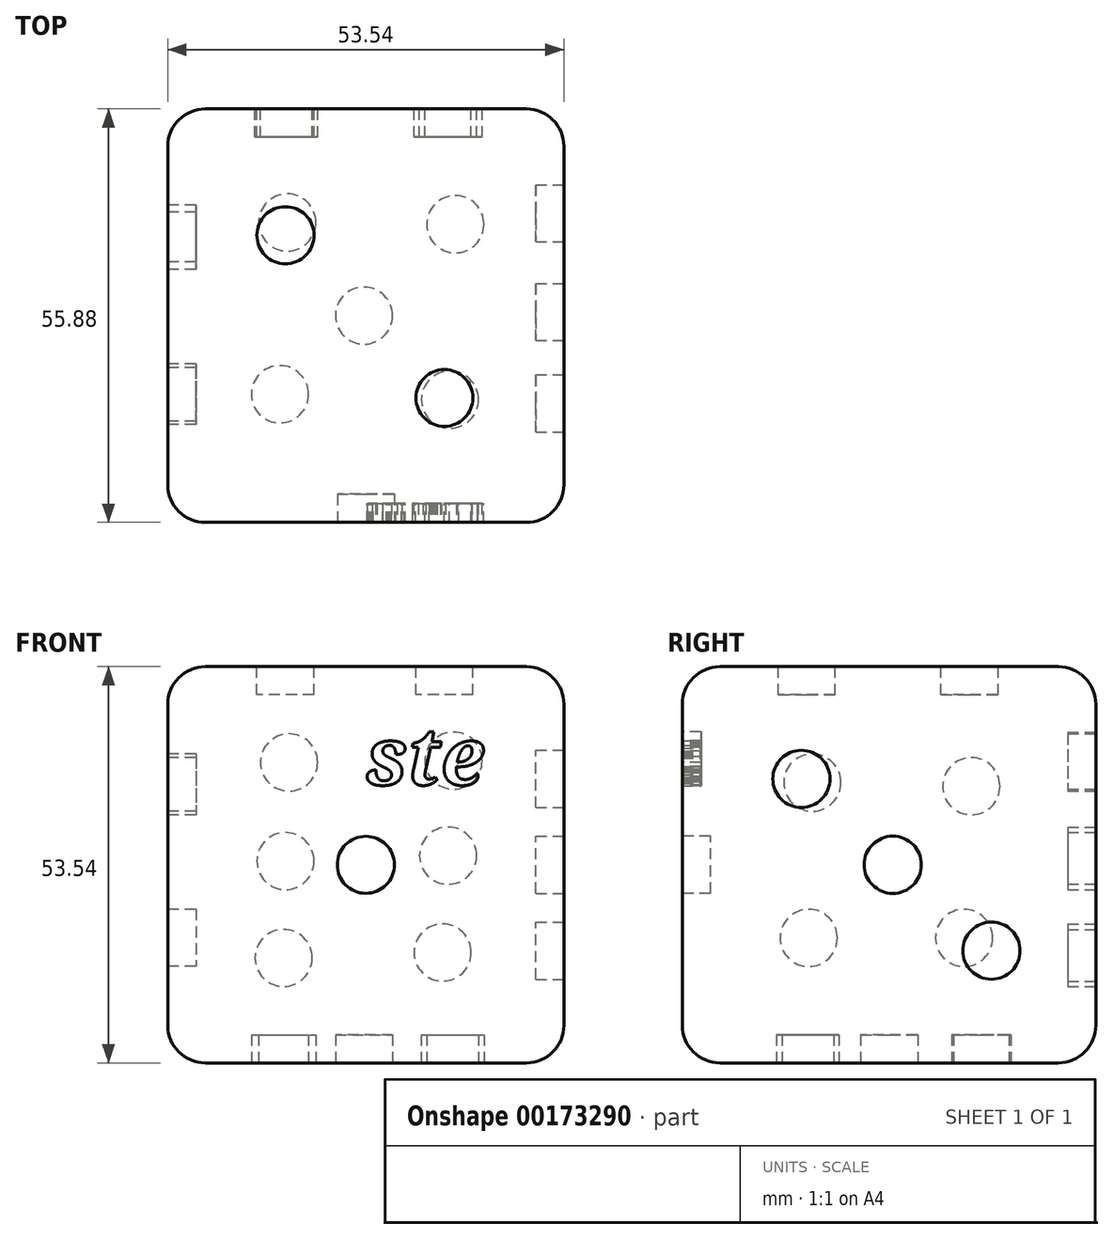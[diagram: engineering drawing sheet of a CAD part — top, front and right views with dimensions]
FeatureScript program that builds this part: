
annotation { "Feature Type Name" : "Feature", "Feature Type Description" : "" }
export const myFeature = defineFeature(function(context is Context, id is Id, definition is map)
    precondition{}
    {
        {
            var Q0;
            Q0=qCreatedBy(makeId("Front.planeOp"),FACE);
            var sketch = newSketch(context, id + "F0", { "sketchPlane" : qUnion([Q0])});
            skCircle(sketch, "E0.cCircle", {"center": v(0, 0) * mm, "radius": 26.77 * mm, "construction": true});
            skLineSegment(sketch, "E0.0", {"start": v(26.77, 26.77) * mm, "end": v(26.77, -26.77) * mm});
            skLineSegment(sketch, "E0.1", {"start": v(26.77, -26.77) * mm, "end": v(-26.77, -26.77) * mm});
            skLineSegment(sketch, "E0.2", {"start": v(-26.77, -26.77) * mm, "end": v(-26.77, 26.77) * mm});
            skLineSegment(sketch, "E0.3", {"start": v(-26.77, 26.77) * mm, "end": v(26.77, 26.77) * mm});
            skPoint(sketch, "E0.0.midPoint", {"position": v(26.77, 0) * mm});
            skSolve(sketch);
        }
        {
            var Q0;
            Q0 = qSketchRegion(id + "F0", true);
            extrude(context, id + "F1", {"entities" : qUnion([Q0]), "endBound" : BoundingType.SYMMETRIC, "depth" : 55.88 * mm});
        }
        {
            var Q0;
            Q0=makeQuery(id+"F1.opExtrude","SWEPT_FACE",FACE,{"disambiguationData":[OSD([sQuery(id+"F0.wireOp",EDGE,"E0.2")])]});
            var Q1;
            Q1=makeQuery(id+"F1.opExtrude","SWEPT_FACE",FACE,{"disambiguationData":[OSD([sQuery(id+"F0.wireOp",EDGE,"E0.1")])]});
            var Q2;
            Q2=makeQuery(id+"F1.opExtrude","CAP_FACE",FACE,{"disambiguationData":[OSD([sQuery(id+"F0.wireOp",EDGE,"E0.0"),sQuery(id+"F0.wireOp",EDGE,"E0.1"),sQuery(id+"F0.wireOp",EDGE,"E0.2"),sQuery(id+"F0.wireOp",EDGE,"E0.3")])],"isStart":false});
            var Q3;
            Q3=makeQuery(id+"F1.opExtrude","SWEPT_FACE",FACE,{"disambiguationData":[OSD([sQuery(id+"F0.wireOp",EDGE,"E0.3")])]});
            var Q4;
            Q4=makeQuery(id+"F1.opExtrude","CAP_FACE",FACE,{"disambiguationData":[OSD([sQuery(id+"F0.wireOp",EDGE,"E0.0"),sQuery(id+"F0.wireOp",EDGE,"E0.1"),sQuery(id+"F0.wireOp",EDGE,"E0.2"),sQuery(id+"F0.wireOp",EDGE,"E0.3")])],"isStart":true});
            fillet(context, id + "F2", {"entities" : qUnion([Q0, Q1, Q2, Q3, Q4]), "radius" : 5.08 * mm, "tangentPropagation" : true, "allowEdgeOverflow" : false});
        }
        {
            var Q0;
            Q0=makeQuery(id+"F1.opExtrude","CAP_FACE",FACE,{"disambiguationData":[OSD([sQuery(id+"F0.wireOp",EDGE,"E0.0"),sQuery(id+"F0.wireOp",EDGE,"E0.1"),sQuery(id+"F0.wireOp",EDGE,"E0.2"),sQuery(id+"F0.wireOp",EDGE,"E0.3")])],"isStart":false});
            var sketch = newSketch(context, id + "F3", { "sketchPlane" : qUnion([Q0])});
            skCircle(sketch, "E1", {"center": v(0, 0) * mm, "radius": 3.86 * mm});
            skSolve(sketch);
        }
        {
            var Q0;
            Q0 = qSketchRegion(id + "F3", true);
            extrude(context, id + "F4", {"entities" : qUnion([Q0]), "operationType" : NewBodyOperationType.REMOVE, "oppositeDirection" : true, "depth" : 3.8 * mm});
        }
        {
            var Q0;
            Q0=makeQuery(id+"F1.opExtrude","SWEPT_FACE",FACE,{"disambiguationData":[OSD([sQuery(id+"F0.wireOp",EDGE,"E0.3")])]});
            var sketch = newSketch(context, id + "F5", { "sketchPlane" : qUnion([Q0])});
            skCircle(sketch, "E2", {"center": v(-10.87, 10.87) * mm, "radius": 3.86 * mm});
            skCircle(sketch, "E3", {"center": v(10.62, -11.11) * mm, "radius": 3.84 * mm});
            skSolve(sketch);
        }
        {
            var Q0;
            Q0 = qSketchRegion(id + "F5", true);
            extrude(context, id + "F6", {"entities" : qUnion([Q0]), "operationType" : NewBodyOperationType.REMOVE, "oppositeDirection" : true, "depth" : 3.8 * mm});
        }
        {
            var Q0;
            Q0=makeQuery(id+"F1.opExtrude","SWEPT_FACE",FACE,{"disambiguationData":[OSD([sQuery(id+"F0.wireOp",EDGE,"E0.0")])]});
            var sketch = newSketch(context, id + "F7", { "sketchPlane" : qUnion([Q0])});
            skCircle(sketch, "E4", {"center": v(-11.85, 11.6) * mm, "radius": 3.87 * mm});
            skCircle(sketch, "E5", {"center": v(0.5, 0) * mm, "radius": 3.87 * mm});
            skCircle(sketch, "E6", {"center": v(13.83, -11.6) * mm, "radius": 3.87 * mm});
            skSolve(sketch);
        }
        {
            var Q0;
            Q0=makeQuery(id+"F7.imprint","IMPRINT",FACE,{"disambiguationData":[TD([[makeQuery(id+"F7.imprint","IMPRINT",EDGE,{"derivedFrom":sQuery(id+"F7.wireOp",EDGE,"E4")}),1.0]])]});
            var Q1;
            Q1=makeQuery(id+"F7.imprint","IMPRINT",FACE,{"disambiguationData":[TD([[makeQuery(id+"F7.imprint","IMPRINT",EDGE,{"derivedFrom":sQuery(id+"F7.wireOp",EDGE,"E5")}),1.0]])]});
            var Q2;
            Q2=makeQuery(id+"F7.imprint","IMPRINT",FACE,{"disambiguationData":[TD([[makeQuery(id+"F7.imprint","IMPRINT",EDGE,{"derivedFrom":sQuery(id+"F7.wireOp",EDGE,"E6")}),1.0]])]});
            var Q3;
            Q3=sQuery(id+"F7.wireOp",EDGE,"E6");
            var Q4;
            Q4=sQuery(id+"F7.wireOp",EDGE,"E4");
            var Q5;
            Q5=sQuery(id+"F7.wireOp",EDGE,"E5");
            extrude(context, id + "F8", {"entities" : qUnion([Q0, Q1, Q2]), "operationType" : NewBodyOperationType.REMOVE, "surfaceEntities" : qUnion([Q3, Q4, Q5]), "oppositeDirection" : true, "depth" : 3.8 * mm});
        }
        {
            var Q0;
            Q0=makeQuery(id+"F1.opExtrude","SWEPT_FACE",FACE,{"disambiguationData":[OSD([sQuery(id+"F0.wireOp",EDGE,"E0.2")])]});
            var sketch = newSketch(context, id + "F9", { "sketchPlane" : qUnion([Q0])});
            skCircle(sketch, "E7", {"center": v(-11.11, 10.62) * mm, "radius": 3.87 * mm});
            skCircle(sketch, "E8", {"center": v(10.37, 11.11) * mm, "radius": 3.87 * mm});
            skCircle(sketch, "E9", {"center": v(-10.12, -9.88) * mm, "radius": 3.87 * mm});
            skCircle(sketch, "E10", {"center": v(10.87, -9.88) * mm, "radius": 3.87 * mm});
            skSolve(sketch);
        }
        {
            var Q0;
            Q0=makeQuery(id+"F9.imprint","IMPRINT",FACE,{"disambiguationData":[TD([[makeQuery(id+"F9.imprint","IMPRINT",EDGE,{"derivedFrom":sQuery(id+"F9.wireOp",EDGE,"E7")}),1.0]])]});
            var Q1;
            Q1=makeQuery(id+"F9.imprint","IMPRINT",FACE,{"disambiguationData":[TD([[makeQuery(id+"F9.imprint","IMPRINT",EDGE,{"derivedFrom":sQuery(id+"F9.wireOp",EDGE,"E8")}),1.0]])]});
            var Q2;
            Q2=makeQuery(id+"F9.imprint","IMPRINT",FACE,{"disambiguationData":[TD([[makeQuery(id+"F9.imprint","IMPRINT",EDGE,{"derivedFrom":sQuery(id+"F9.wireOp",EDGE,"E9")}),1.0]])]});
            var Q3;
            Q3=makeQuery(id+"F9.imprint","IMPRINT",FACE,{"disambiguationData":[TD([[makeQuery(id+"F9.imprint","IMPRINT",EDGE,{"derivedFrom":sQuery(id+"F9.wireOp",EDGE,"E10")}),1.0]])]});
            var Q4;
            Q4=sQuery(id+"F9.wireOp",EDGE,"E10");
            var Q5;
            Q5=sQuery(id+"F9.wireOp",EDGE,"E8");
            extrude(context, id + "F10", {"entities" : qUnion([Q0, Q1, Q2, Q3]), "operationType" : NewBodyOperationType.REMOVE, "surfaceEntities" : qUnion([Q4, Q5]), "oppositeDirection" : true, "depth" : 3.8 * mm});
        }
        {
            var Q0;
            Q0=makeQuery(id+"F1.opExtrude","SWEPT_FACE",FACE,{"disambiguationData":[OSD([sQuery(id+"F0.wireOp",EDGE,"E0.1")])]});
            var sketch = newSketch(context, id + "F11", { "sketchPlane" : qUnion([Q0])});
            skCircle(sketch, "E11", {"center": v(-11.6, 10.62) * mm, "radius": 3.87 * mm});
            skCircle(sketch, "E12", {"center": v(11.36, 11.36) * mm, "radius": 3.87 * mm});
            skCircle(sketch, "E13", {"center": v(-10.62, -12.6) * mm, "radius": 3.87 * mm});
            skCircle(sketch, "E14", {"center": v(-0.25, 0) * mm, "radius": 3.87 * mm});
            skCircle(sketch, "E15", {"center": v(12.1, -12.35) * mm, "radius": 3.87 * mm});
            skSolve(sketch);
        }
        {
            var Q0;
            Q0=makeQuery(id+"F11.imprint","IMPRINT",FACE,{"disambiguationData":[TD([[makeQuery(id+"F11.imprint","IMPRINT",EDGE,{"derivedFrom":sQuery(id+"F11.wireOp",EDGE,"E11")}),1.0]])]});
            var Q1;
            Q1=makeQuery(id+"F11.imprint","IMPRINT",FACE,{"disambiguationData":[TD([[makeQuery(id+"F11.imprint","IMPRINT",EDGE,{"derivedFrom":sQuery(id+"F11.wireOp",EDGE,"E12")}),1.0]])]});
            var Q2;
            Q2=makeQuery(id+"F11.imprint","IMPRINT",FACE,{"disambiguationData":[TD([[makeQuery(id+"F11.imprint","IMPRINT",EDGE,{"derivedFrom":sQuery(id+"F11.wireOp",EDGE,"E14")}),1.0]])]});
            var Q3;
            Q3=makeQuery(id+"F11.imprint","IMPRINT",FACE,{"disambiguationData":[TD([[makeQuery(id+"F11.imprint","IMPRINT",EDGE,{"derivedFrom":sQuery(id+"F11.wireOp",EDGE,"E13")}),1.0]])]});
            var Q4;
            Q4=makeQuery(id+"F11.imprint","IMPRINT",FACE,{"disambiguationData":[TD([[makeQuery(id+"F11.imprint","IMPRINT",EDGE,{"derivedFrom":sQuery(id+"F11.wireOp",EDGE,"E15")}),1.0]])]});
            var Q5;
            Q5=sQuery(id+"F11.wireOp",EDGE,"E15");
            var Q6;
            Q6=sQuery(id+"F11.wireOp",EDGE,"E11");
            var Q7;
            Q7=sQuery(id+"F11.wireOp",EDGE,"E12");
            var Q8;
            Q8=sQuery(id+"F11.wireOp",EDGE,"E14");
            var Q9;
            Q9=sQuery(id+"F11.wireOp",EDGE,"E13");
            extrude(context, id + "F12", {"entities" : qUnion([Q0, Q1, Q2, Q3, Q4]), "operationType" : NewBodyOperationType.REMOVE, "surfaceEntities" : qUnion([Q5, Q6, Q7, Q8, Q9]), "oppositeDirection" : true, "depth" : 3.8 * mm});
        }
        {
            var Q0;
            Q0=makeQuery(id+"F1.opExtrude","CAP_FACE",FACE,{"disambiguationData":[OSD([sQuery(id+"F0.wireOp",EDGE,"E0.0"),sQuery(id+"F0.wireOp",EDGE,"E0.1"),sQuery(id+"F0.wireOp",EDGE,"E0.2"),sQuery(id+"F0.wireOp",EDGE,"E0.3")])],"isStart":true});
            var sketch = newSketch(context, id + "F13", { "sketchPlane" : qUnion([Q0])});
            skCircle(sketch, "E16", {"center": v(-11.85, 14.08) * mm, "radius": 3.87 * mm});
            skCircle(sketch, "E17", {"center": v(-11.11, 1.23) * mm, "radius": 3.87 * mm});
            skCircle(sketch, "E18", {"center": v(-10.37, -11.85) * mm, "radius": 3.87 * mm});
            skCircle(sketch, "E19", {"center": v(10.37, 13.83) * mm, "radius": 3.87 * mm});
            skCircle(sketch, "E20", {"center": v(10.87, 0.5) * mm, "radius": 3.87 * mm});
            skCircle(sketch, "E21", {"center": v(11.11, -12.6) * mm, "radius": 3.87 * mm});
            skSolve(sketch);
        }
        {
            var Q0;
            Q0=makeQuery(id+"F13.imprint","IMPRINT",FACE,{"disambiguationData":[TD([[makeQuery(id+"F13.imprint","IMPRINT",EDGE,{"derivedFrom":sQuery(id+"F13.wireOp",EDGE,"E16")}),1.0]])]});
            var Q1;
            Q1=makeQuery(id+"F13.imprint","IMPRINT",FACE,{"disambiguationData":[TD([[makeQuery(id+"F13.imprint","IMPRINT",EDGE,{"derivedFrom":sQuery(id+"F13.wireOp",EDGE,"E17")}),1.0]])]});
            var Q2;
            Q2=makeQuery(id+"F13.imprint","IMPRINT",FACE,{"disambiguationData":[TD([[makeQuery(id+"F13.imprint","IMPRINT",EDGE,{"derivedFrom":sQuery(id+"F13.wireOp",EDGE,"E18")}),1.0]])]});
            var Q3;
            Q3=makeQuery(id+"F13.imprint","IMPRINT",FACE,{"disambiguationData":[TD([[makeQuery(id+"F13.imprint","IMPRINT",EDGE,{"derivedFrom":sQuery(id+"F13.wireOp",EDGE,"E21")}),1.0]])]});
            var Q4;
            Q4=makeQuery(id+"F13.imprint","IMPRINT",FACE,{"disambiguationData":[TD([[makeQuery(id+"F13.imprint","IMPRINT",EDGE,{"derivedFrom":sQuery(id+"F13.wireOp",EDGE,"E20")}),1.0]])]});
            var Q5;
            Q5=makeQuery(id+"F13.imprint","IMPRINT",FACE,{"disambiguationData":[TD([[makeQuery(id+"F13.imprint","IMPRINT",EDGE,{"derivedFrom":sQuery(id+"F13.wireOp",EDGE,"E19")}),1.0]])]});
            var Q6;
            Q6=sQuery(id+"F13.wireOp",EDGE,"E21");
            extrude(context, id + "F14", {"entities" : qUnion([Q0, Q1, Q2, Q3, Q4, Q5]), "operationType" : NewBodyOperationType.REMOVE, "surfaceEntities" : qUnion([Q6]), "oppositeDirection" : true, "depth" : 3.8 * mm});
        }
        {
            var Q0;
            Q0=makeQuery(id+"F1.opExtrude","CAP_FACE",FACE,{"disambiguationData":[OSD([sQuery(id+"F0.wireOp",EDGE,"E0.0"),sQuery(id+"F0.wireOp",EDGE,"E0.1"),sQuery(id+"F0.wireOp",EDGE,"E0.2"),sQuery(id+"F0.wireOp",EDGE,"E0.3")])],"isStart":false});
            var sketch = newSketch(context, id + "F15", { "sketchPlane" : qUnion([Q0])});
            skText(sketch, "E22", { "text": "ste", "fontName": "NotoSerif-BoldItalic.ttf"});
            const initialGuessF15  = {"E22": [0, 0.0108, 1, 0, 0.00784]};
            skSetInitialGuess(sketch, initialGuessF15);
            skSolve(sketch);
        }
        {
            var Q0;
            Q0 = qSketchRegion(id + "F15", true);
            extrude(context, id + "F16", {"entities" : qUnion([Q0]), "operationType" : NewBodyOperationType.REMOVE, "oppositeDirection" : true, "depth" : 2.54 * mm});
        }
    });
